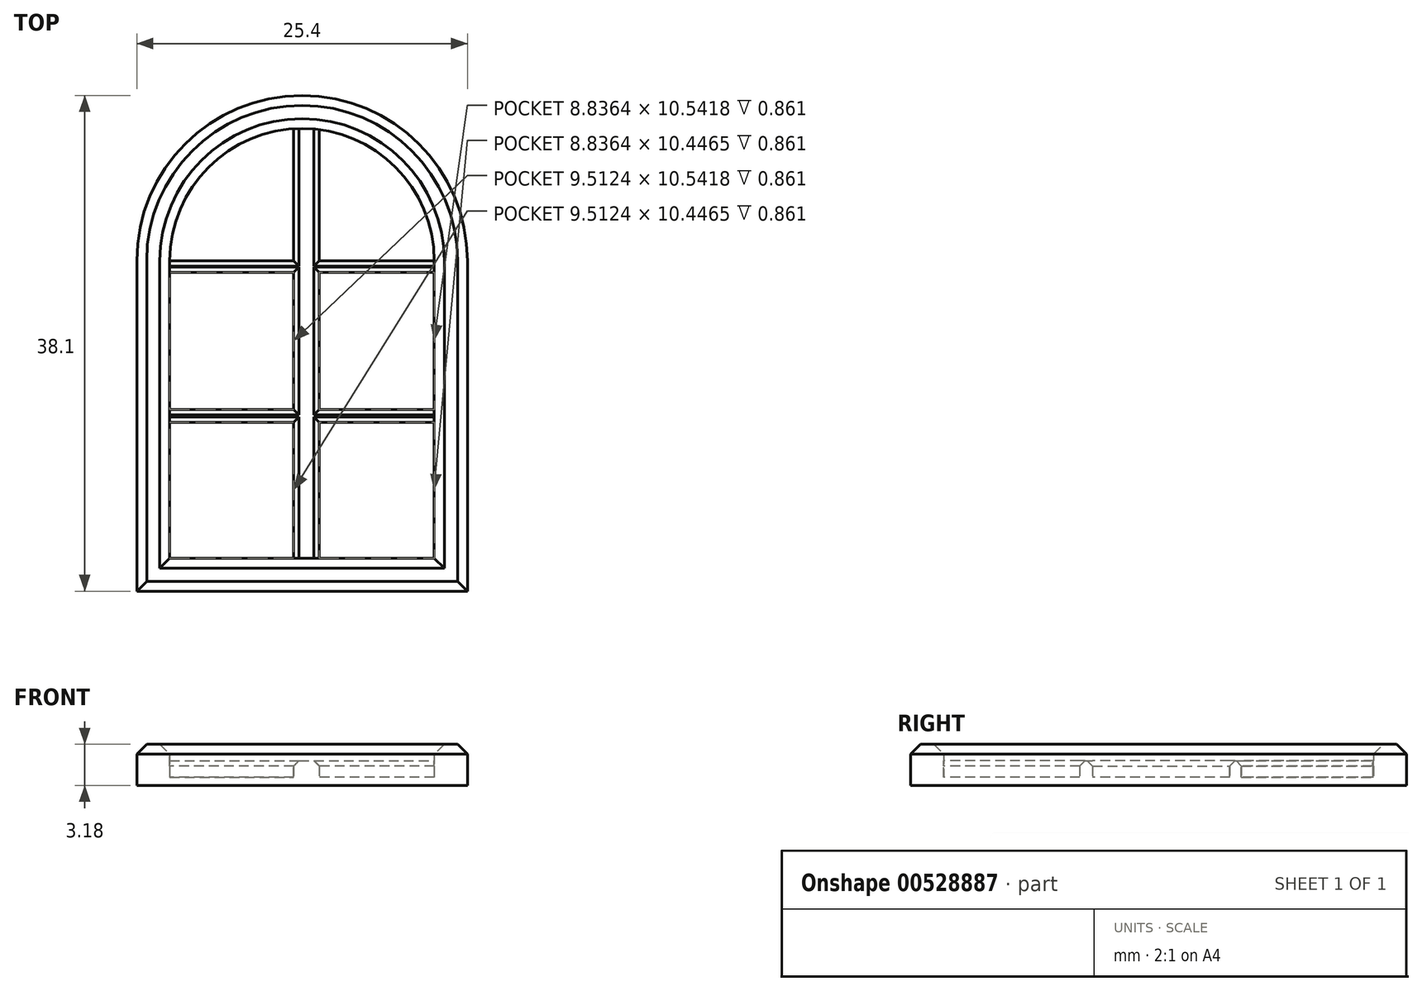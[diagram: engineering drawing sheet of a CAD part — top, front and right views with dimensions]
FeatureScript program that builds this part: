
annotation { "Feature Type Name" : "Feature", "Feature Type Description" : "" }
export const myFeature = defineFeature(function(context is Context, id is Id, definition is map)
    precondition{}
    {
        {
            var Q0;
            Q0=qCreatedBy(makeId("Top.planeOp"),FACE);
            var sketch = newSketch(context, id + "F0", { "sketchPlane" : qUnion([Q0])});
            skLineSegment(sketch, "E0.bottom", {"start": v(-41.61, -53.73) * mm, "end": v(-16.21, -53.73) * mm});
            skLineSegment(sketch, "E0.top", {"start": v(-41.61, -28.33) * mm, "end": v(-16.21, -28.33) * mm});
            skLineSegment(sketch, "E0.left", {"start": v(-41.61, -53.73) * mm, "end": v(-41.61, -28.33) * mm});
            skLineSegment(sketch, "E0.right", {"start": v(-16.21, -53.73) * mm, "end": v(-16.21, -28.33) * mm});
            skArc(sketch, "E1", {"start": v(-16.21, -28.33) * mm, "mid": v(-28.91, -15.63) * mm, "end": v(-41.61, -28.33) * mm});
            skSolve(sketch);
        }
        {
            var Q0;
            Q0 = qSketchRegion(id + "F0", true);
            extrude(context, id + "F1", {"entities" : qUnion([Q0]), "depth" : 3.17 * mm, "offsetDistance" : 25.4 * mm});
        }
        {
            var Q0;
            Q0=makeQuery(id+"F1.opExtrude","CAP_FACE",FACE,{"disambiguationData":[OSD([sQuery(id+"F0.wireOp",EDGE,"E0.bottom"),sQuery(id+"F0.wireOp",EDGE,"E0.left"),sQuery(id+"F0.wireOp",EDGE,"E0.right"),sQuery(id+"F0.wireOp",EDGE,"E1")])],"isStart":false});
            shell(context, id + "F2", {"entities" : qUnion([Q0]), "thickness" : 2.54 * mm});
        }
        {
            var Q0;
            Q0=makeQuery(id+"F2.opShell","OFFSET_FACE",FACE,{"disambiguationData":[OSD([sQuery(id+"F0.wireOp",EDGE,"E0.bottom"),sQuery(id+"F0.wireOp",EDGE,"E0.left"),sQuery(id+"F0.wireOp",EDGE,"E0.right"),sQuery(id+"F0.wireOp",EDGE,"E1")])]});
            extrude(context, id + "F3", {"entities" : qUnion([Q0]), "operationType" : NewBodyOperationType.REMOVE, "oppositeDirection" : true, "depth" : 1.9 * mm, "offsetDistance" : 25.4 * mm});
        }
        {
            var Q0;
            Q0=makeQuery(id+"F3.boolean.opBoolean","COPY",FACE,{"derivedFrom":makeQuery(id+"F3.opExtrude","CAP_FACE",FACE,{"disambiguationData":[OSD([sQuery(id+"F0.wireOp",EDGE,"E0.bottom"),sQuery(id+"F0.wireOp",EDGE,"E0.left"),sQuery(id+"F0.wireOp",EDGE,"E0.right"),sQuery(id+"F0.wireOp",EDGE,"E1")])],"isStart":false})});
            var sketch = newSketch(context, id + "F4", { "sketchPlane" : qUnion([Q0])});
            skLineSegment(sketch, "E2.bottom", {"start": v(-18.75, -28.33) * mm, "end": v(-39.07, -28.33) * mm});
            skLineSegment(sketch, "E2.top", {"start": v(-18.75, -29.22) * mm, "end": v(-39.07, -29.22) * mm});
            skLineSegment(sketch, "E2.left", {"start": v(-18.75, -28.33) * mm, "end": v(-18.75, -29.22) * mm});
            skLineSegment(sketch, "E2.right", {"start": v(-39.07, -28.33) * mm, "end": v(-39.07, -29.22) * mm});
            skLineSegment(sketch, "E3.bottom", {"start": v(-29.58, -51.2) * mm, "end": v(-28.08, -51.2) * mm});
            skLineSegment(sketch, "E3.top", {"start": v(-29.58, -18.2) * mm, "end": v(-28.08, -18.2) * mm});
            skLineSegment(sketch, "E3.left", {"start": v(-29.58, -51.2) * mm, "end": v(-29.58, -18.2) * mm});
            skLineSegment(sketch, "E3.right", {"start": v(-28.08, -51.2) * mm, "end": v(-28.08, -18.2) * mm});
            skLineSegment(sketch, "E4.bottom", {"start": v(-39.07, -39.76) * mm, "end": v(-18.75, -39.76) * mm});
            skLineSegment(sketch, "E4.top", {"start": v(-39.07, -40.75) * mm, "end": v(-18.75, -40.75) * mm});
            skLineSegment(sketch, "E4.left", {"start": v(-39.07, -39.76) * mm, "end": v(-39.07, -40.75) * mm});
            skLineSegment(sketch, "E4.right", {"start": v(-18.75, -39.76) * mm, "end": v(-18.75, -40.75) * mm});
            skSolve(sketch);
        }
        {
            var Q0;
            {var subQ5=sQuery(id+"F4.wireOp",EDGE,"E4.left");Q0=makeQuery(id+"F4.imprint","IMPRINT",FACE,{"disambiguationData":[TD([[makeQuery(id+"F4.imprint","IMPRINT",EDGE,{"derivedFrom":subQ5}),-1.0]])]});}
            var Q1;
            {var subQ0=sQuery(id+"F4.wireOp",EDGE,"E4.top");var subQ1=sQuery(id+"F4.wireOp",EDGE,"E3.left");var subQ2=makeQuery(id+"F4.imprint","INTERSECT",VERTEX,{"derivedFrom":[subQ1,subQ0]});Q1=makeQuery(id+"F4.imprint","IMPRINT",FACE,{"disambiguationData":[TD([[makeQuery(id+"F4.imprint","IMPRINT",EDGE,{"disambiguationData":[TD([[subQ2,-1.0]])],"derivedFrom":subQ1}),-1.0]])]});}
            var Q2;
            {var subQ5=sQuery(id+"F4.wireOp",EDGE,"E4.right");Q2=makeQuery(id+"F4.imprint","IMPRINT",FACE,{"disambiguationData":[TD([[makeQuery(id+"F4.imprint","IMPRINT",EDGE,{"derivedFrom":subQ5}),1.0]])]});}
            var Q3;
            {var subQ0=sQuery(id+"F4.wireOp",EDGE,"E2.left");Q3=makeQuery(id+"F4.imprint","IMPRINT",FACE,{"disambiguationData":[TD([[makeQuery(id+"F4.imprint","IMPRINT",EDGE,{"derivedFrom":subQ0}),1.0]])]});}
            var Q4;
            {var subQ0=sQuery(id+"F4.wireOp",EDGE,"E3.right");var subQ1=sQuery(id+"F4.wireOp",EDGE,"E2.bottom");var subQ2=makeQuery(id+"F4.imprint","INTERSECT",VERTEX,{"derivedFrom":[subQ1,subQ0]});Q4=makeQuery(id+"F4.imprint","IMPRINT",FACE,{"disambiguationData":[TD([[makeQuery(id+"F4.imprint","IMPRINT",EDGE,{"disambiguationData":[TD([[subQ2,-1.0]])],"derivedFrom":subQ1}),1.0]])]});}
            var Q5;
            {var subQ0=sQuery(id+"F4.wireOp",EDGE,"E2.right");Q5=makeQuery(id+"F4.imprint","IMPRINT",FACE,{"disambiguationData":[TD([[makeQuery(id+"F4.imprint","IMPRINT",EDGE,{"derivedFrom":subQ0}),-1.0]])]});}
            extrude(context, id + "F5", {"entities" : qUnion([Q0, Q1, Q2, Q3, Q4, Q5]), "operationType" : NewBodyOperationType.ADD, "depth" : 1.27 * mm, "offsetDistance" : 25.4 * mm});
        }
        {
            var Q0;
            {var subQ0=sQuery(id+"F0.wireOp",EDGE,"E0.bottom");Q0=makeQuery(id+"F3.boolean.opBoolean","MERGE",FACE,{"derivedFrom":[makeQuery(id+"F2.opShell","OFFSET_FACE",FACE,{"disambiguationData":[OSD([subQ0])]}),makeQuery(id+"F3.opExtrude","SWEPT_FACE",FACE,{"disambiguationData":[OSD([subQ0])]})]});}
            var sketch = newSketch(context, id + "F6", { "sketchPlane" : qUnion([Q0])});
            skLineSegment(sketch, "E5.bottom", {"start": v(29.56, 0.64) * mm, "end": v(27.6, 0.64) * mm});
            skLineSegment(sketch, "E5.top", {"start": v(29.56, 1.9) * mm, "end": v(27.6, 1.9) * mm});
            skLineSegment(sketch, "E5.left", {"start": v(29.56, 0.64) * mm, "end": v(29.56, 1.9) * mm});
            skLineSegment(sketch, "E5.right", {"start": v(27.6, 0.64) * mm, "end": v(27.6, 1.9) * mm});
            skSolve(sketch);
        }
        {
            var Q0;
            Q0 = qSketchRegion(id + "F6", true);
            extrude(context, id + "F7", {"entities" : qUnion([Q0]), "operationType" : NewBodyOperationType.ADD, "depth" : 33.02 * mm, "offsetDistance" : 25.4 * mm});
        }
        {
            var Q0;
            {var subQ0=sQuery(id+"F4.wireOp",EDGE,"E4.top");var subQ1=makeQuery(id+"F5.opExtrude","SWEPT_FACE",FACE,{"disambiguationData":[OSD([subQ0])]});var subQ2=makeQuery(id+"F5.opExtrude","CAP_FACE",FACE,{"disambiguationData":[OSD([sQuery(id+"F4.wireOp",EDGE,"E4.bottom"),subQ0,sQuery(id+"F4.wireOp",EDGE,"E4.left"),sQuery(id+"F4.wireOp",EDGE,"E4.right")])],"isStart":false});var subQ3=sQuery(id+"F0.wireOp",EDGE,"E0.left");Q0=makeQuery(id+"F7.boolean.opBoolean","SPLIT",EDGE,{"disambiguationData":[topologyDisambiguationEdgeConnected([subQ2,subQ1]),TD([makeQuery(id+"F2.opShell","OFFSET_FACE",FACE,{"disambiguationData":[OSD([subQ3])]})])],"derivedFrom":makeQuery(id+"F5.opExtrude","CAP_EDGE",EDGE,{"disambiguationData":[OSD([subQ0])],"isStart":false})});}
            var Q1;
            {var subQ0=sQuery(id+"F4.wireOp",EDGE,"E4.top");var subQ1=makeQuery(id+"F5.opExtrude","SWEPT_FACE",FACE,{"disambiguationData":[OSD([subQ0])]});var subQ2=makeQuery(id+"F5.opExtrude","CAP_FACE",FACE,{"disambiguationData":[OSD([sQuery(id+"F4.wireOp",EDGE,"E4.bottom"),subQ0,sQuery(id+"F4.wireOp",EDGE,"E4.left"),sQuery(id+"F4.wireOp",EDGE,"E4.right")])],"isStart":false});var subQ3=sQuery(id+"F0.wireOp",EDGE,"E0.right");Q1=makeQuery(id+"F7.boolean.opBoolean","SPLIT",EDGE,{"disambiguationData":[topologyDisambiguationEdgeConnected([subQ2,subQ1]),TD([makeQuery(id+"F2.opShell","OFFSET_FACE",FACE,{"disambiguationData":[OSD([subQ3])]})])],"derivedFrom":makeQuery(id+"F5.opExtrude","CAP_EDGE",EDGE,{"disambiguationData":[OSD([subQ0])],"isStart":false})});}
            var Q2;
            {var subQ0=sQuery(id+"F4.wireOp",EDGE,"E4.bottom");var subQ1=makeQuery(id+"F5.opExtrude","SWEPT_FACE",FACE,{"disambiguationData":[OSD([subQ0])]});var subQ2=makeQuery(id+"F5.opExtrude","CAP_FACE",FACE,{"disambiguationData":[OSD([subQ0,sQuery(id+"F4.wireOp",EDGE,"E4.top"),sQuery(id+"F4.wireOp",EDGE,"E4.left"),sQuery(id+"F4.wireOp",EDGE,"E4.right")])],"isStart":false});var subQ3=sQuery(id+"F0.wireOp",EDGE,"E0.right");Q2=makeQuery(id+"F7.boolean.opBoolean","SPLIT",EDGE,{"disambiguationData":[topologyDisambiguationEdgeConnected([subQ1,subQ2]),TD([makeQuery(id+"F2.opShell","OFFSET_FACE",FACE,{"disambiguationData":[OSD([subQ3])]})])],"derivedFrom":makeQuery(id+"F5.opExtrude","CAP_EDGE",EDGE,{"disambiguationData":[OSD([subQ0])],"isStart":false})});}
            var Q3;
            {var subQ0=sQuery(id+"F4.wireOp",EDGE,"E2.top");var subQ1=makeQuery(id+"F5.opExtrude","CAP_FACE",FACE,{"disambiguationData":[OSD([sQuery(id+"F4.wireOp",EDGE,"E2.bottom"),subQ0,sQuery(id+"F4.wireOp",EDGE,"E2.left"),sQuery(id+"F4.wireOp",EDGE,"E2.right")])],"isStart":false});var subQ2=makeQuery(id+"F5.opExtrude","SWEPT_FACE",FACE,{"disambiguationData":[OSD([subQ0])]});var subQ3=sQuery(id+"F0.wireOp",EDGE,"E0.right");Q3=makeQuery(id+"F7.boolean.opBoolean","SPLIT",EDGE,{"disambiguationData":[topologyDisambiguationEdgeConnected([subQ1,subQ2]),TD([makeQuery(id+"F2.opShell","OFFSET_FACE",FACE,{"disambiguationData":[OSD([subQ3])]})])],"derivedFrom":makeQuery(id+"F5.opExtrude","CAP_EDGE",EDGE,{"disambiguationData":[OSD([subQ0])],"isStart":false})});}
            var Q4;
            {var subQ1=sQuery(id+"F0.wireOp",EDGE,"E0.right");var subQ2=sQuery(id+"F4.wireOp",EDGE,"E2.bottom");var subQ3=makeQuery(id+"F5.opExtrude","SWEPT_FACE",FACE,{"disambiguationData":[OSD([subQ2])]});var subQ4=makeQuery(id+"F5.opExtrude","CAP_FACE",FACE,{"disambiguationData":[OSD([subQ2,sQuery(id+"F4.wireOp",EDGE,"E2.top"),sQuery(id+"F4.wireOp",EDGE,"E2.left"),sQuery(id+"F4.wireOp",EDGE,"E2.right")])],"isStart":false});Q4=makeQuery(id+"F7.boolean.opBoolean","SPLIT",EDGE,{"disambiguationData":[topologyDisambiguationEdgeConnected([subQ3,subQ4]),TD([makeQuery(id+"F2.opShell","OFFSET_FACE",FACE,{"disambiguationData":[OSD([subQ1])]})])],"derivedFrom":makeQuery(id+"F5.opExtrude","CAP_EDGE",EDGE,{"disambiguationData":[OSD([subQ2])],"isStart":false})});}
            var Q5;
            {var subQ1=sQuery(id+"F0.wireOp",EDGE,"E0.left");var subQ2=sQuery(id+"F4.wireOp",EDGE,"E2.bottom");var subQ3=makeQuery(id+"F5.opExtrude","SWEPT_FACE",FACE,{"disambiguationData":[OSD([subQ2])]});var subQ4=makeQuery(id+"F5.opExtrude","CAP_FACE",FACE,{"disambiguationData":[OSD([subQ2,sQuery(id+"F4.wireOp",EDGE,"E2.top"),sQuery(id+"F4.wireOp",EDGE,"E2.left"),sQuery(id+"F4.wireOp",EDGE,"E2.right")])],"isStart":false});Q5=makeQuery(id+"F7.boolean.opBoolean","SPLIT",EDGE,{"disambiguationData":[topologyDisambiguationEdgeConnected([subQ3,subQ4]),TD([makeQuery(id+"F2.opShell","OFFSET_FACE",FACE,{"disambiguationData":[OSD([subQ1])]})])],"derivedFrom":makeQuery(id+"F5.opExtrude","CAP_EDGE",EDGE,{"disambiguationData":[OSD([subQ2])],"isStart":false})});}
            var Q6;
            {var subQ0=sQuery(id+"F4.wireOp",EDGE,"E2.top");var subQ1=makeQuery(id+"F5.opExtrude","SWEPT_FACE",FACE,{"disambiguationData":[OSD([subQ0])]});var subQ2=makeQuery(id+"F5.opExtrude","CAP_FACE",FACE,{"disambiguationData":[OSD([sQuery(id+"F4.wireOp",EDGE,"E2.bottom"),subQ0,sQuery(id+"F4.wireOp",EDGE,"E2.left"),sQuery(id+"F4.wireOp",EDGE,"E2.right")])],"isStart":false});var subQ3=sQuery(id+"F0.wireOp",EDGE,"E0.left");Q6=makeQuery(id+"F7.boolean.opBoolean","SPLIT",EDGE,{"disambiguationData":[topologyDisambiguationEdgeConnected([subQ2,subQ1]),TD([makeQuery(id+"F2.opShell","OFFSET_FACE",FACE,{"disambiguationData":[OSD([subQ3])]})])],"derivedFrom":makeQuery(id+"F5.opExtrude","CAP_EDGE",EDGE,{"disambiguationData":[OSD([subQ0])],"isStart":false})});}
            var Q7;
            {var subQ0=sQuery(id+"F4.wireOp",EDGE,"E4.bottom");var subQ1=makeQuery(id+"F5.opExtrude","CAP_FACE",FACE,{"disambiguationData":[OSD([subQ0,sQuery(id+"F4.wireOp",EDGE,"E4.top"),sQuery(id+"F4.wireOp",EDGE,"E4.left"),sQuery(id+"F4.wireOp",EDGE,"E4.right")])],"isStart":false});var subQ2=makeQuery(id+"F5.opExtrude","SWEPT_FACE",FACE,{"disambiguationData":[OSD([subQ0])]});var subQ3=sQuery(id+"F0.wireOp",EDGE,"E0.left");Q7=makeQuery(id+"F7.boolean.opBoolean","SPLIT",EDGE,{"disambiguationData":[topologyDisambiguationEdgeConnected([subQ2,subQ1]),TD([makeQuery(id+"F2.opShell","OFFSET_FACE",FACE,{"disambiguationData":[OSD([subQ3])]})])],"derivedFrom":makeQuery(id+"F5.opExtrude","CAP_EDGE",EDGE,{"disambiguationData":[OSD([subQ0])],"isStart":false})});}
            var Q8;
            {var subQ1=sQuery(id+"F6.wireOp",EDGE,"E5.top");var subQ2=sQuery(id+"F4.wireOp",EDGE,"E2.top");var subQ3=sQuery(id+"F6.wireOp",EDGE,"E5.left");Q8=makeQuery(id+"F7.boolean.opBoolean","SPLIT",EDGE,{"disambiguationData":[TD([makeQuery(id+"F5.opExtrude","SWEPT_FACE",FACE,{"disambiguationData":[OSD([subQ2])]})])],"derivedFrom":makeQuery(id+"F7.opExtrude","SWEPT_EDGE",EDGE,{"disambiguationData":[OSD([subQ1,subQ3])]})});}
            var Q9;
            {var subQ1=sQuery(id+"F6.wireOp",EDGE,"E5.top");var subQ2=sQuery(id+"F4.wireOp",EDGE,"E2.top");var subQ3=sQuery(id+"F6.wireOp",EDGE,"E5.right");Q9=makeQuery(id+"F7.boolean.opBoolean","SPLIT",EDGE,{"disambiguationData":[TD([makeQuery(id+"F5.opExtrude","SWEPT_FACE",FACE,{"disambiguationData":[OSD([subQ2])]})])],"derivedFrom":makeQuery(id+"F7.opExtrude","SWEPT_EDGE",EDGE,{"disambiguationData":[OSD([subQ1,subQ3])]})});}
            var Q10;
            {var subQ1=sQuery(id+"F6.wireOp",EDGE,"E5.left");var subQ2=sQuery(id+"F6.wireOp",EDGE,"E5.top");var subQ3=sQuery(id+"F0.wireOp",EDGE,"E0.bottom");Q10=makeQuery(id+"F7.boolean.opBoolean","SPLIT",EDGE,{"disambiguationData":[TD([makeQuery(id+"F2.opShell","OFFSET_FACE",FACE,{"disambiguationData":[OSD([subQ3])]})])],"derivedFrom":makeQuery(id+"F7.opExtrude","SWEPT_EDGE",EDGE,{"disambiguationData":[OSD([subQ2,subQ1])]})});}
            var Q11;
            {var subQ1=sQuery(id+"F6.wireOp",EDGE,"E5.top");var subQ2=sQuery(id+"F0.wireOp",EDGE,"E0.bottom");var subQ3=sQuery(id+"F6.wireOp",EDGE,"E5.right");Q11=makeQuery(id+"F7.boolean.opBoolean","SPLIT",EDGE,{"disambiguationData":[TD([makeQuery(id+"F2.opShell","OFFSET_FACE",FACE,{"disambiguationData":[OSD([subQ2])]})])],"derivedFrom":makeQuery(id+"F7.opExtrude","SWEPT_EDGE",EDGE,{"disambiguationData":[OSD([subQ1,subQ3])]})});}
            var Q12;
            {var subQ1=sQuery(id+"F0.wireOp",EDGE,"E1");var subQ2=sQuery(id+"F6.wireOp",EDGE,"E5.left");var subQ3=sQuery(id+"F6.wireOp",EDGE,"E5.top");Q12=makeQuery(id+"F7.boolean.opBoolean","SPLIT",EDGE,{"disambiguationData":[TD([makeQuery(id+"F2.opShell","OFFSET_FACE",FACE,{"disambiguationData":[OSD([subQ1])]})])],"derivedFrom":makeQuery(id+"F7.opExtrude","SWEPT_EDGE",EDGE,{"disambiguationData":[OSD([subQ3,subQ2])]})});}
            var Q13;
            {var subQ1=sQuery(id+"F0.wireOp",EDGE,"E1");var subQ2=sQuery(id+"F6.wireOp",EDGE,"E5.top");var subQ3=sQuery(id+"F6.wireOp",EDGE,"E5.right");Q13=makeQuery(id+"F7.boolean.opBoolean","SPLIT",EDGE,{"disambiguationData":[TD([makeQuery(id+"F2.opShell","OFFSET_FACE",FACE,{"disambiguationData":[OSD([subQ1])]})])],"derivedFrom":makeQuery(id+"F7.opExtrude","SWEPT_EDGE",EDGE,{"disambiguationData":[OSD([subQ2,subQ3])]})});}
            chamfer(context, id + "F8", {"entities" : qUnion([Q0, Q1, Q2, Q3, Q4, Q5, Q6, Q7, Q8, Q9, Q10, Q11, Q12, Q13]), "width" : 0.4 * mm, "tangentPropagation" : true});
        }
        {
            var Q0;
            {var subQ0=sQuery(id+"F0.wireOp",EDGE,"E1");Q0=makeQuery(id+"F2.opShell","OFFSET_EDGE",EDGE,{"disambiguationData":[OSD([subQ0]),TDD([makeQuery(id+"F1.opExtrude","CAP_EDGE",EDGE,{"disambiguationData":[OSD([subQ0])],"isStart":false})])]});}
            var Q1;
            {var subQ0=sQuery(id+"F0.wireOp",EDGE,"E0.right");Q1=makeQuery(id+"F2.opShell","OFFSET_EDGE",EDGE,{"disambiguationData":[OSD([subQ0]),TDD([makeQuery(id+"F1.opExtrude","CAP_EDGE",EDGE,{"disambiguationData":[OSD([subQ0])],"isStart":false})])]});}
            var Q2;
            {var subQ0=sQuery(id+"F0.wireOp",EDGE,"E0.bottom");Q2=makeQuery(id+"F2.opShell","OFFSET_EDGE",EDGE,{"disambiguationData":[OSD([subQ0]),TDD([makeQuery(id+"F1.opExtrude","CAP_EDGE",EDGE,{"disambiguationData":[OSD([subQ0])],"isStart":false})])]});}
            var Q3;
            {var subQ0=sQuery(id+"F0.wireOp",EDGE,"E0.left");Q3=makeQuery(id+"F2.opShell","OFFSET_EDGE",EDGE,{"disambiguationData":[OSD([subQ0]),TDD([makeQuery(id+"F1.opExtrude","CAP_EDGE",EDGE,{"disambiguationData":[OSD([subQ0])],"isStart":false})])]});}
            var Q4;
            Q4=makeQuery(id+"F1.opExtrude","CAP_EDGE",EDGE,{"disambiguationData":[OSD([sQuery(id+"F0.wireOp",EDGE,"E1")])],"isStart":false});
            var Q5;
            Q5=makeQuery(id+"F1.opExtrude","CAP_EDGE",EDGE,{"disambiguationData":[OSD([sQuery(id+"F0.wireOp",EDGE,"E0.bottom")])],"isStart":false});
            chamfer(context, id + "F9", {"entities" : qUnion([Q0, Q1, Q2, Q3, Q4, Q5]), "width" : 0.76 * mm, "tangentPropagation" : true});
        }
    });
